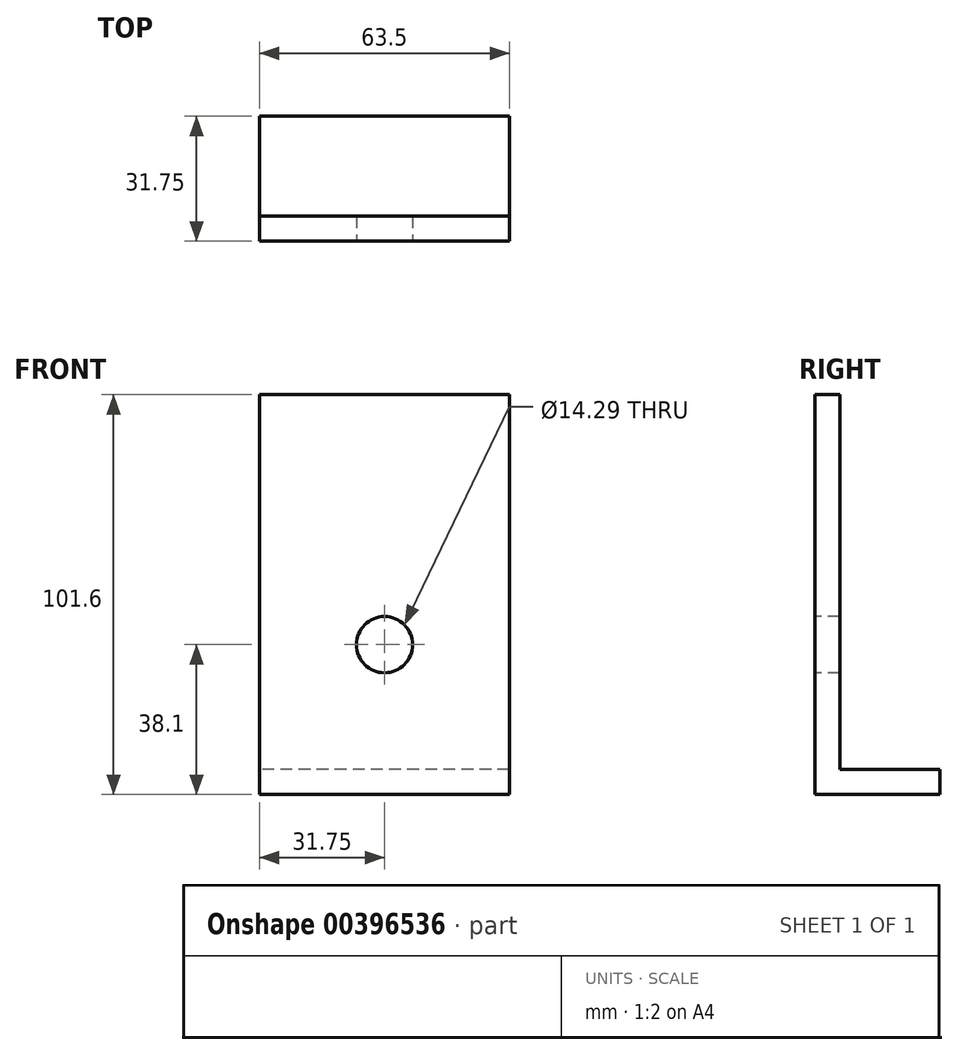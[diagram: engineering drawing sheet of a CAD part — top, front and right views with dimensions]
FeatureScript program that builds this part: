
annotation { "Feature Type Name" : "Feature", "Feature Type Description" : "" }
export const myFeature = defineFeature(function(context is Context, id is Id, definition is map)
    precondition{}
    {
        {
            var Q0;
            Q0=qCreatedBy(makeId("Right.planeOp"),FACE);
            var sketch = newSketch(context, id + "F0", { "sketchPlane" : qUnion([Q0])});
            skLineSegment(sketch, "E0", {"start": v(0, 0) * mm, "end": v(31.75, 0) * mm});
            skLineSegment(sketch, "E1", {"start": v(31.75, 0) * mm, "end": v(31.75, 6.35) * mm});
            skLineSegment(sketch, "E2", {"start": v(31.75, 6.35) * mm, "end": v(6.35, 6.35) * mm});
            skLineSegment(sketch, "E3", {"start": v(6.35, 6.35) * mm, "end": v(6.35, 101.6) * mm});
            skLineSegment(sketch, "E4", {"start": v(6.35, 101.6) * mm, "end": v(0, 101.6) * mm});
            skLineSegment(sketch, "E5", {"start": v(0, 101.6) * mm, "end": v(0, 0) * mm});
            skSolve(sketch);
        }
        {
            var Q0;
            Q0=makeQuery(id+"F0.imprint","IMPRINT",FACE,{"disambiguationData":[TD([[makeQuery(id+"F0.imprint","IMPRINT",EDGE,{"derivedFrom":sQuery(id+"F0.wireOp",EDGE,"E0")}),1.0]])]});
            extrude(context, id + "F1", {"entities" : qUnion([Q0]), "depth" : 63.5 * mm});
        }
        {
            var Q0;
            Q0=makeQuery(id+"F1.opExtrude","SWEPT_FACE",FACE,{"disambiguationData":[OSD([sQuery(id+"F0.wireOp",EDGE,"E5")])]});
            var sketch = newSketch(context, id + "F2", { "sketchPlane" : qUnion([Q0])});
            skCircle(sketch, "E6", {"center": v(31.75, 38.1) * mm, "radius": 7.14 * mm});
            skSolve(sketch);
        }
        {
            var Q0;
            Q0=sQuery(id+"F2.wireOp",VERTEX,"E6.center");
            var Q1;
            Q1=makeQuery(id+"F1.opExtrude","SWEPT_BODY",BODY,{"disambiguationData":[OSD([sQuery(id+"F0.wireOp",EDGE,"E0"),sQuery(id+"F0.wireOp",EDGE,"E1"),sQuery(id+"F0.wireOp",EDGE,"E2"),sQuery(id+"F0.wireOp",EDGE,"E3"),sQuery(id+"F0.wireOp",EDGE,"E4"),sQuery(id+"F0.wireOp",EDGE,"E5")])]});
            hole(context, id + "F3", {"style" : HoleStyle.SIMPLE, "endStyle" : HoleEndStyle.THROUGH, "holeDiameter" : 14.29 * mm, "isTappedThrough" : true, "tappedDepth" : 12.7 * mm, "tapClearance" : 3, "locations" : qUnion([Q0]), "scope" : qUnion([Q1])});
        }
    });
